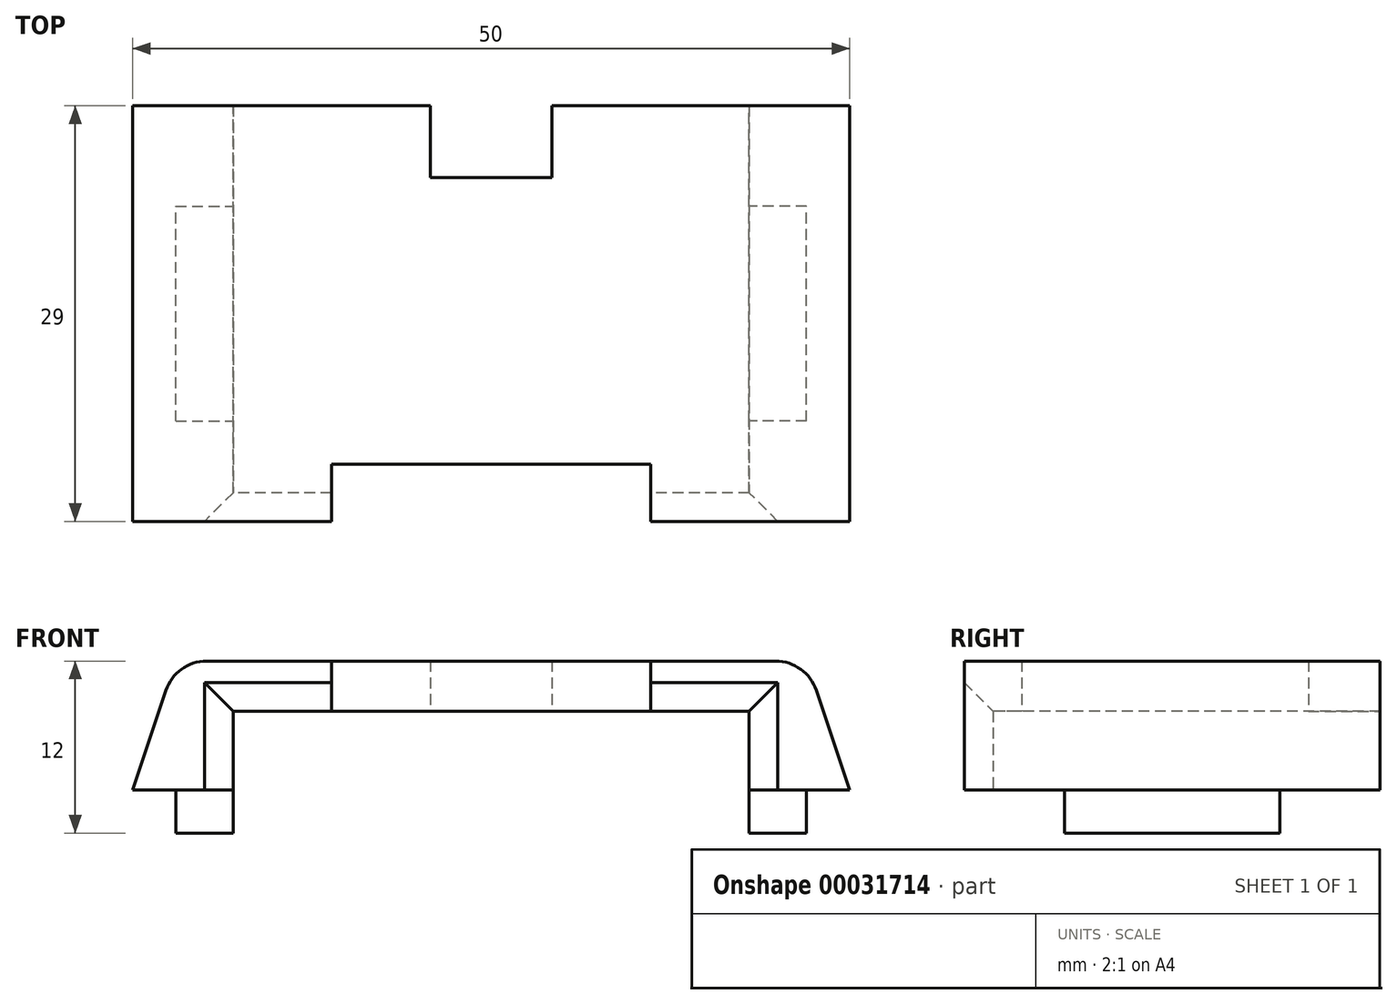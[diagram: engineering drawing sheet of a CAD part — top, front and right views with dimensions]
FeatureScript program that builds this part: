
annotation { "Feature Type Name" : "Feature", "Feature Type Description" : "" }
export const myFeature = defineFeature(function(context is Context, id is Id, definition is map)
    precondition{}
    {
        {
            var Q0;
            Q0=qCreatedBy(makeId("Top.planeOp"),FACE);
            var sketch = newSketch(context, id + "F0", { "sketchPlane" : qUnion([Q0])});
            skLineSegment(sketch, "E0", {"start": v(-18, 12.15) * mm, "end": v(-4.25, 12.15) * mm});
            skLineSegment(sketch, "E1", {"start": v(-4.25, 12.15) * mm, "end": v(-4.25, 7.15) * mm});
            skLineSegment(sketch, "E2", {"start": v(-4.25, 7.15) * mm, "end": v(4.25, 7.15) * mm});
            skLineSegment(sketch, "E3", {"start": v(4.25, 7.15) * mm, "end": v(4.25, 12.15) * mm});
            skLineSegment(sketch, "E4", {"start": v(4.25, 12.15) * mm, "end": v(18, 12.15) * mm});
            skLineSegment(sketch, "E5", {"start": v(18, 12.15) * mm, "end": v(18, -16.85) * mm});
            skLineSegment(sketch, "E6", {"start": v(18, -16.85) * mm, "end": v(11.12, -16.85) * mm});
            skLineSegment(sketch, "E7", {"start": v(11.12, -16.85) * mm, "end": v(11.12, -12.85) * mm});
            skLineSegment(sketch, "E8", {"start": v(11.12, -12.85) * mm, "end": v(-11.12, -12.85) * mm});
            skLineSegment(sketch, "E9", {"start": v(-11.12, -12.85) * mm, "end": v(-11.12, -16.85) * mm});
            skLineSegment(sketch, "E10", {"start": v(-11.12, -16.85) * mm, "end": v(-18, -16.85) * mm});
            skLineSegment(sketch, "E11", {"start": v(-18, -16.85) * mm, "end": v(-18, 12.15) * mm});
            skSolve(sketch);
        }
        {
            var Q0;
            Q0 = qSketchRegion(id + "F0", true);
            extrude(context, id + "F1", {"entities" : qUnion([Q0]), "depth" : 3.5 * mm});
        }
        {
            var Q0;
            Q0=makeQuery(id+"F1.opExtrude","SWEPT_FACE",FACE,{"disambiguationData":[OSD([sQuery(id+"F0.wireOp",EDGE,"E11")])]});
            var sketch = newSketch(context, id + "F2", { "sketchPlane" : qUnion([Q0])});
            skLineSegment(sketch, "E12.bottom", {"start": v(-12.15, 3.5) * mm, "end": v(16.85, 3.5) * mm});
            skLineSegment(sketch, "E12.top", {"start": v(-12.15, -5.5) * mm, "end": v(16.85, -5.5) * mm});
            skLineSegment(sketch, "E12.left", {"start": v(-12.15, 3.5) * mm, "end": v(-12.15, -5.5) * mm});
            skLineSegment(sketch, "E12.right", {"start": v(16.85, 3.5) * mm, "end": v(16.85, -5.5) * mm});
            skSolve(sketch);
        }
        {
            var Q0;
            Q0 = qSketchRegion(id + "F2", true);
            extrude(context, id + "F3", {"entities" : qUnion([Q0]), "operationType" : NewBodyOperationType.ADD, "depth" : 4 * mm});
        }
        {
            var Q0;
            Q0=makeQuery(id+"F1.opExtrude","SWEPT_FACE",FACE,{"disambiguationData":[OSD([sQuery(id+"F0.wireOp",EDGE,"E5")])]});
            var sketch = newSketch(context, id + "F4", { "sketchPlane" : qUnion([Q0])});
            skLineSegment(sketch, "E13.bottom", {"start": v(-16.85, 3.5) * mm, "end": v(12.15, 3.5) * mm});
            skLineSegment(sketch, "E13.top", {"start": v(-16.85, -5.5) * mm, "end": v(12.15, -5.5) * mm});
            skLineSegment(sketch, "E13.left", {"start": v(-16.85, 3.5) * mm, "end": v(-16.85, -5.5) * mm});
            skLineSegment(sketch, "E13.right", {"start": v(12.15, 3.5) * mm, "end": v(12.15, -5.5) * mm});
            skSolve(sketch);
        }
        {
            var Q0;
            Q0 = qSketchRegion(id + "F4", true);
            extrude(context, id + "F5", {"entities" : qUnion([Q0]), "operationType" : NewBodyOperationType.ADD, "depth" : 4 * mm});
        }
        {
            var Q0;
            Q0=makeQuery(id+"F1.opExtrude","CAP_EDGE",EDGE,{"disambiguationData":[OSD([sQuery(id+"F0.wireOp",EDGE,"E10")])],"isStart":true});
            var Q1;
            Q1=makeQuery(id+"F1.opExtrude","CAP_EDGE",EDGE,{"disambiguationData":[OSD([sQuery(id+"F0.wireOp",EDGE,"E6")])],"isStart":true});
            chamfer(context, id + "F6", {"entities" : qUnion([Q0, Q1]), "width" : 2 * mm, "tangentPropagation" : true});
        }
        {
            var Q0;
            Q0=makeQuery(id+"F5.opExtrude","SWEPT_FACE",FACE,{"disambiguationData":[OSD([sQuery(id+"F4.wireOp",EDGE,"E13.top")])]});
            var sketch = newSketch(context, id + "F7", { "sketchPlane" : qUnion([Q0])});
            skLineSegment(sketch, "E14.bottom", {"start": v(22, -5.15) * mm, "end": v(18, -5.15) * mm});
            skLineSegment(sketch, "E14.top", {"start": v(22, 9.85) * mm, "end": v(18, 9.85) * mm});
            skLineSegment(sketch, "E14.left", {"start": v(22, -5.15) * mm, "end": v(22, 9.85) * mm});
            skLineSegment(sketch, "E14.right", {"start": v(18, -5.15) * mm, "end": v(18, 9.85) * mm});
            skLineSegment(sketch, "E15", {"start": v(41.9, 2.35) * mm, "end": v(-44.93, 2.35) * mm, "construction": true});
            skLineSegment(sketch, "E16.bottom", {"start": v(-22, -5.15) * mm, "end": v(-18, -5.15) * mm});
            skLineSegment(sketch, "E16.top", {"start": v(-22, 9.85) * mm, "end": v(-18, 9.85) * mm});
            skLineSegment(sketch, "E16.left", {"start": v(-22, -5.15) * mm, "end": v(-22, 9.85) * mm});
            skLineSegment(sketch, "E16.right", {"start": v(-18, -5.15) * mm, "end": v(-18, 9.85) * mm});
            skSolve(sketch);
        }
        {
            var Q0;
            Q0 = qSketchRegion(id + "F7", true);
            extrude(context, id + "F8", {"entities" : qUnion([Q0]), "operationType" : NewBodyOperationType.ADD, "depth" : 3 * mm});
        }
        {
            var Q0;
            Q0=makeQuery(id+"F5.opExtrude","CAP_EDGE",EDGE,{"disambiguationData":[OSD([sQuery(id+"F4.wireOp",EDGE,"E13.left")])],"isStart":true});
            var Q1;
            Q1=makeQuery(id+"F3.opExtrude","CAP_EDGE",EDGE,{"disambiguationData":[OSD([sQuery(id+"F2.wireOp",EDGE,"E12.right")])],"isStart":true});
            chamfer(context, id + "F9", {"entities" : qUnion([Q0, Q1]), "width" : 2 * mm, "tangentPropagation" : true});
        }
        {
            var Q0;
            Q0=makeQuery(id+"F3.boolean.opBoolean","MERGE",FACE,{"derivedFrom":[makeQuery(id+"F1.opExtrude","SWEPT_FACE",FACE,{"disambiguationData":[OSD([sQuery(id+"F0.wireOp",EDGE,"E0")])]}),makeQuery(id+"F3.opExtrude","SWEPT_FACE",FACE,{"disambiguationData":[OSD([sQuery(id+"F2.wireOp",EDGE,"E12.left")])]})]});
            var sketch = newSketch(context, id + "F10", { "sketchPlane" : qUnion([Q0])});
            skLineSegment(sketch, "E17", {"start": v(22, 3.5) * mm, "end": v(22, -5.5) * mm});
            skLineSegment(sketch, "E18", {"start": v(22, -5.5) * mm, "end": v(25, -5.5) * mm});
            skLineSegment(sketch, "E19", {"start": v(25, -5.5) * mm, "end": v(22, 3.5) * mm});
            skLineSegment(sketch, "E20", {"start": v(0, 10.19) * mm, "end": v(0, -17.52) * mm, "construction": true});
            skLineSegment(sketch, "E21.MirrorCS", {"start": v(-22, 3.5) * mm, "end": v(-22, -5.5) * mm});
            skLineSegment(sketch, "E22.MirrorCS", {"start": v(-22, -5.5) * mm, "end": v(-25, -5.5) * mm});
            skLineSegment(sketch, "E23.MirrorCS", {"start": v(-25, -5.5) * mm, "end": v(-22, 3.5) * mm});
            skSolve(sketch);
        }
        {
            var Q0;
            Q0 = qSketchRegion(id + "F10", true);
            var Q1;
            Q1=makeQuery(id+"F3.boolean.opBoolean","MERGE",FACE,{"derivedFrom":[makeQuery(id+"F1.opExtrude","SWEPT_FACE",FACE,{"disambiguationData":[OSD([sQuery(id+"F0.wireOp",EDGE,"E10")])]}),makeQuery(id+"F3.opExtrude","SWEPT_FACE",FACE,{"disambiguationData":[OSD([sQuery(id+"F2.wireOp",EDGE,"E12.right")])]})]});
            extrude(context, id + "F11", {"entities" : qUnion([Q0]), "operationType" : NewBodyOperationType.ADD, "endBound" : BoundingType.UP_TO_SURFACE, "oppositeDirection" : true, "endBoundEntityFace" : qUnion([Q1]), "depth" : 25 * mm});
        }
        {
            var Q0;
            {var subQ0=sQuery(id+"F2.wireOp",EDGE,"E12.bottom");Q0=makeQuery(id+"F11.boolean.opBoolean","MERGE",EDGE,{"derivedFrom":[makeQuery(id+"F3.opExtrude","CAP_EDGE",EDGE,{"disambiguationData":[OSD([subQ0])],"isStart":false}),makeQuery(id+"F11.opExtrude","SWEPT_EDGE",EDGE,{"disambiguationData":[OSD([sQuery(id+"F0.wireOp",EDGE,"E0"),subQ0,sQuery(id+"F2.wireOp",EDGE,"E12.left"),sQuery(id+"F10.wireOp",EDGE,"E17"),sQuery(id+"F10.wireOp",EDGE,"E19")])]})]});}
            var Q1;
            Q1=makeQuery(id+"F11.boolean.opBoolean","MERGE",EDGE,{"derivedFrom":[makeQuery(id+"F5.opExtrude","CAP_EDGE",EDGE,{"disambiguationData":[OSD([sQuery(id+"F4.wireOp",EDGE,"E13.bottom")])],"isStart":false}),makeQuery(id+"F11.opExtrude","SWEPT_EDGE",EDGE,{"disambiguationData":[OSD([sQuery(id+"F10.wireOp",EDGE,"E21.MirrorCS"),sQuery(id+"F10.wireOp",EDGE,"E23.MirrorCS")])]})]});
            fillet(context, id + "F12", {"entities" : qUnion([Q0, Q1]), "radius" : 3 * mm, "tangentPropagation" : true, "allowEdgeOverflow" : false});
        }
    });
